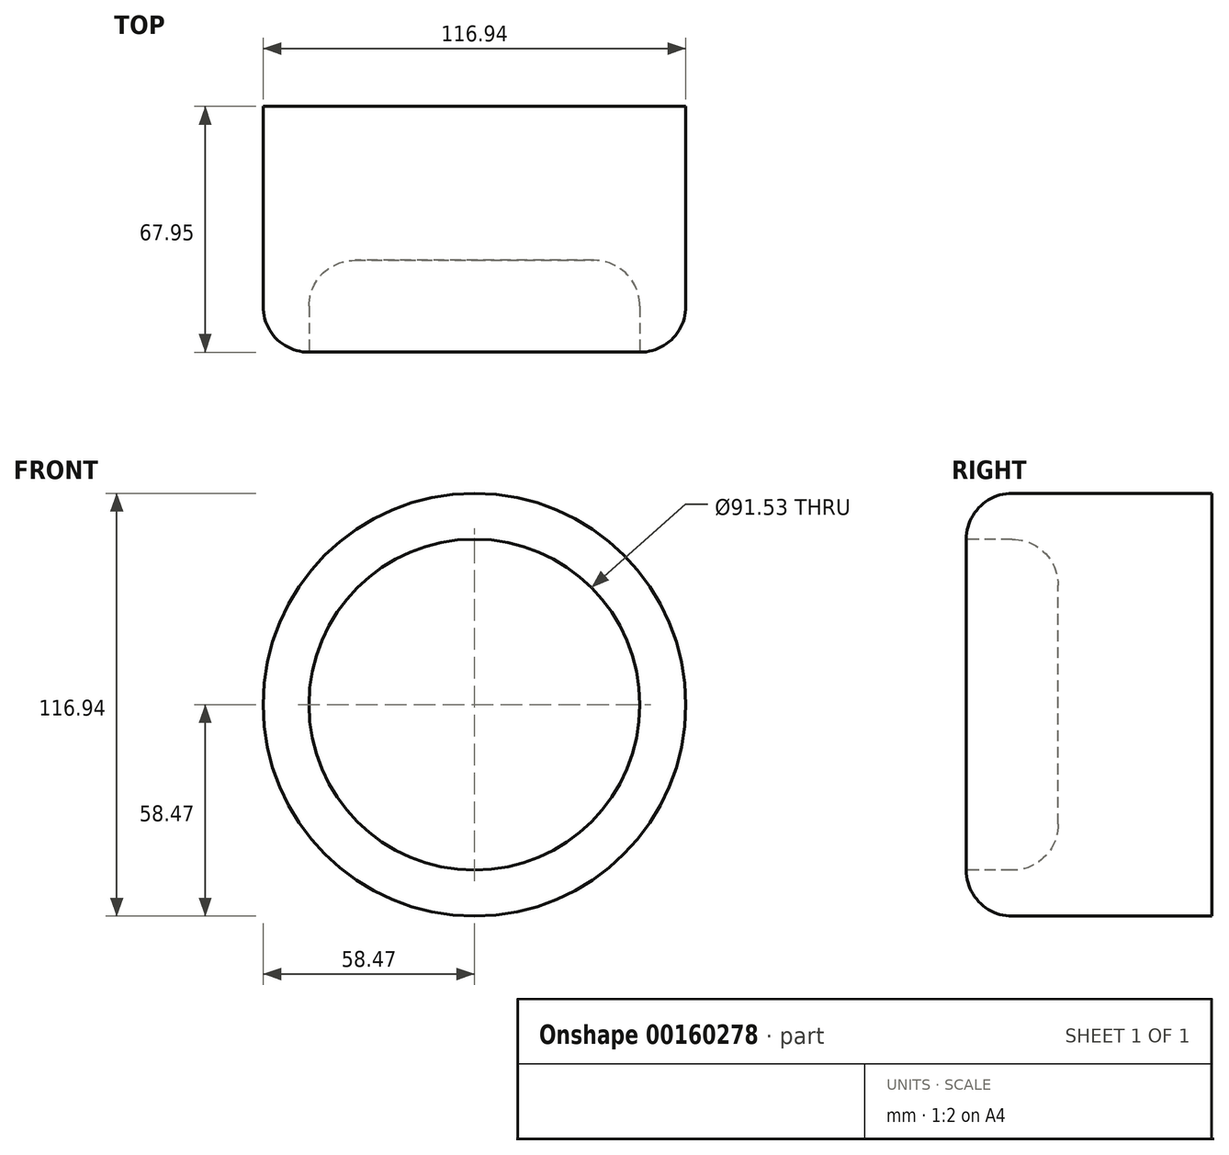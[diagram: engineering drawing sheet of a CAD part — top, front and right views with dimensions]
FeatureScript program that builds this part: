
annotation { "Feature Type Name" : "Feature", "Feature Type Description" : "" }
export const myFeature = defineFeature(function(context is Context, id is Id, definition is map)
    precondition{}
    {
        {
            var Q0;
            Q0=qCreatedBy(makeId("Front.planeOp"),FACE);
            var sketch = newSketch(context, id + "F0", { "sketchPlane" : qUnion([Q0])});
            skCircle(sketch, "E0", {"center": v(0, 0) * mm, "radius": 58.47 * mm});
            skSolve(sketch);
        }
        {
            var Q0;
            Q0=makeQuery(id+"F0.imprint","IMPRINT",FACE,{"disambiguationData":[TD([[makeQuery(id+"F0.imprint","IMPRINT",EDGE,{"derivedFrom":sQuery(id+"F0.wireOp",EDGE,"E0")}),1.0]])]});
            extrude(context, id + "F1", {"entities" : qUnion([Q0]), "depth" : 67.94 * mm});
        }
        {
            var Q0;
            Q0=makeQuery(id+"F1.opExtrude","CAP_FACE",FACE,{"disambiguationData":[OSD([sQuery(id+"F0.wireOp",EDGE,"E0")])],"isStart":false});
            fillet(context, id + "F2", {"entities" : qUnion([Q0]), "radius" : 12.7 * mm, "tangentPropagation" : true, "allowEdgeOverflow" : false});
        }
        {
            var Q0;
            Q0=makeQuery(id+"F1.opExtrude","CAP_FACE",FACE,{"disambiguationData":[OSD([sQuery(id+"F0.wireOp",EDGE,"E0")])],"isStart":false});
            var sketch = newSketch(context, id + "F3", { "sketchPlane" : qUnion([Q0])});
            skCircle(sketch, "E1", {"center": v(0, 0) * mm, "radius": 18.32 * mm});
            skSolve(sketch);
        }
        {
            var Q0;
            Q0=makeQuery(id+"F3.imprint","IMPRINT",FACE,{"disambiguationData":[TD([[makeQuery(id+"F3.imprint","IMPRINT",EDGE,{"derivedFrom":sQuery(id+"F3.wireOp",EDGE,"E1")}),-1.0]])]});
            var Q1;
            Q1 = qSketchRegion(id + "F3", true);
            extrude(context, id + "F4", {"entities" : qUnion([Q0, Q1]), "operationType" : NewBodyOperationType.REMOVE, "oppositeDirection" : true, "depth" : 25.4 * mm});
        }
        {
            var Q0;
            Q0=makeQuery(id+"F4.boolean.opBoolean","COPY",FACE,{"derivedFrom":makeQuery(id+"F4.opExtrude","CAP_FACE",FACE,{"disambiguationData":[OSD([sQuery(id+"F0.wireOp",EDGE,"E0")])],"isStart":false})});
            fillet(context, id + "F5", {"entities" : qUnion([Q0]), "radius" : 12.7 * mm, "tangentPropagation" : true, "allowEdgeOverflow" : false});
        }
    });
